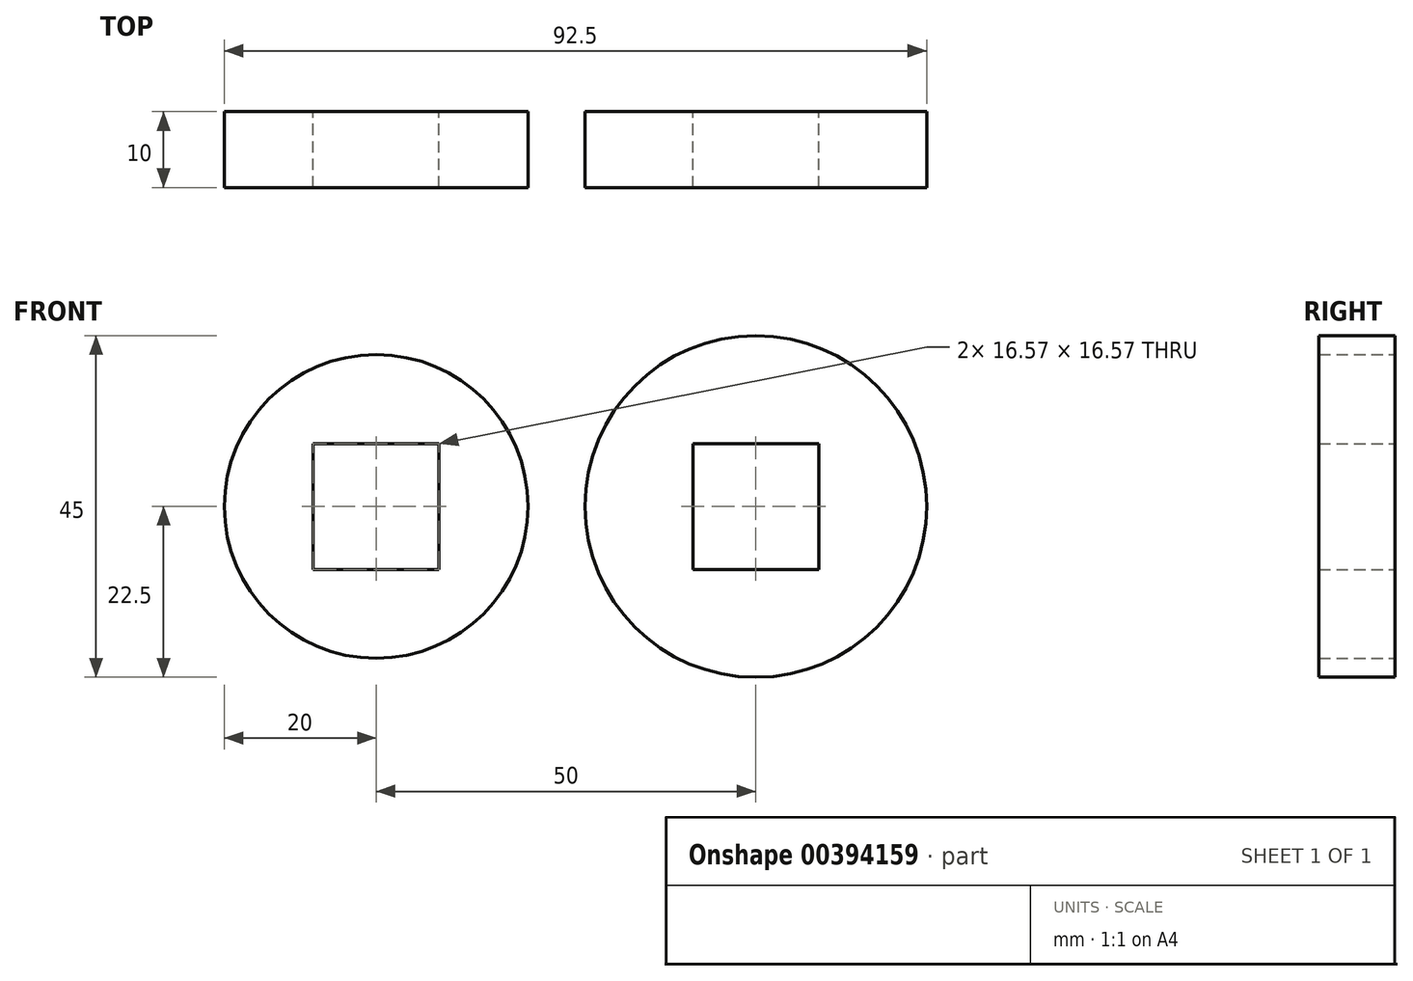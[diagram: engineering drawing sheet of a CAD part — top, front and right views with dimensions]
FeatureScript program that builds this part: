
annotation { "Feature Type Name" : "Feature", "Feature Type Description" : "" }
export const myFeature = defineFeature(function(context is Context, id is Id, definition is map)
    precondition{}
    {
        {
            var Q0;
            Q0=qCreatedBy(makeId("Front.planeOp"),FACE);
            var sketch = newSketch(context, id + "F0", { "sketchPlane" : qUnion([Q0])});
            skCircle(sketch, "E0", {"center": v(0, 0) * mm, "radius": 20 * mm});
            skCircle(sketch, "E1", {"center": v(50, 0) * mm, "radius": 22.5 * mm});
            skLineSegment(sketch, "E2.bottom", {"start": v(-8.28, 8.28) * mm, "end": v(8.28, 8.28) * mm});
            skLineSegment(sketch, "E2.top", {"start": v(-8.28, -8.28) * mm, "end": v(8.28, -8.28) * mm});
            skLineSegment(sketch, "E2.left", {"start": v(-8.28, 8.28) * mm, "end": v(-8.28, -8.28) * mm});
            skLineSegment(sketch, "E2.right", {"start": v(8.28, 8.28) * mm, "end": v(8.28, -8.28) * mm});
            skLineSegment(sketch, "E3.bottom", {"start": v(41.72, 8.28) * mm, "end": v(58.28, 8.28) * mm});
            skLineSegment(sketch, "E3.top", {"start": v(41.72, -8.28) * mm, "end": v(58.28, -8.28) * mm});
            skLineSegment(sketch, "E3.left", {"start": v(41.72, 8.28) * mm, "end": v(41.72, -8.28) * mm});
            skLineSegment(sketch, "E3.right", {"start": v(58.28, 8.28) * mm, "end": v(58.28, -8.28) * mm});
            skSolve(sketch);
        }
        {
            var Q0;
            Q0=makeQuery(id+"F0.imprint","IMPRINT",FACE,{"disambiguationData":[TD([[makeQuery(id+"F0.imprint","IMPRINT",EDGE,{"derivedFrom":sQuery(id+"F0.wireOp",EDGE,"E0")}),1.0]])]});
            var Q1;
            Q1=makeQuery(id+"F0.imprint","IMPRINT",FACE,{"disambiguationData":[TD([[makeQuery(id+"F0.imprint","IMPRINT",EDGE,{"derivedFrom":sQuery(id+"F0.wireOp",EDGE,"E1")}),1.0]])]});
            extrude(context, id + "F1", {"entities" : qUnion([Q0, Q1]), "depth" : 10 * mm});
        }
    });
